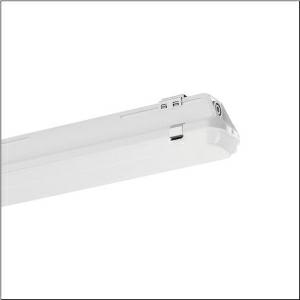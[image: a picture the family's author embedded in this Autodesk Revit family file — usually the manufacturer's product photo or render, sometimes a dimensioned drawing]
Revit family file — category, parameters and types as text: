
# Revit family: monsun_r__12_51fp207p430h_da32
name_source: partatom
category: Lighting Fixtures
units: mm (PartAtom-declared; Revit-internal decimal feet)

## family parameters
Cut with Voids When Loaded = No
Host = Face
Light Source = No
Part Type = Normal
Room Calculation Point = No
Round Connector Dimension = Use Diameter
Shared = No

## types (1)
- Monsun® 12 (1 x LED, 3990 lm, 24.8 W, 4000K)
    Apparent Load = 25 VA
    CIE Flux Codes = 45 75 93 94 100
    Color Rendering = 80
    Color Temperature = 4000K
    Default Elevation = 1800 mm
    Description = Monsun® 12, damp-proof luminaire, chain hanger, primary optical cover: enclosure, of PC, light emission: direct distribution, primary light characteristic: symmetric, installation type: suspended mounting, surface-mounted, horizontal mounting, vertical mounting, LED rated luminous flux: 3.990 lm, light colour: 840, colour temperature: 4000K, control gear: ECG, with terminal, 3-pole, max. 2.5mm², mains connection: 220..240V, AC, 50/60Hz, rated input power: 25W, luminaire housing, of glass-fibre reinforced polyester, uncoated, bright grey, length: 1.590 mm, width: 90 mm, height: 88mm, clip for enclosure, of stainless steel (V2A), ceiling mounting element, of stainless steel (V2A), chain hanger, of stainless steel (V2A), protection rating (complete): IP66, insulation class (complete): insulation class I (protective earthing), certification: CE, ENEC, VDE, protection symbol: D, impact resistance: IK08, permissible ambient temperature for indoor applications: -35..+40°C, standard: EN 50419, EN 60598-2-1, no direct snow, no direct sun, no direct rain, for indoor or canopied outdoor use, corresponds to IFS (International Featured Standards) requirements for safety and quality in the food industry, packaging unit: 1 piece
    Height = 89 mm
    Lamp = 1 x LED
    Lamp Light Flux = 3990 lm
    Lamp Power = 24.8 W
    Lamp count = 1
    Length = 1590 mm
    Luminous efficacy = 161 lm/W
    Manufacturer = Siteco
    ModVariant = No
    Model = 51FP207P430H
    Mounting Place = Ceiling
    Mounting Type = Pendant
    Number of Poles = 1
    OnlyDefault = Yes
    Power Factor = 1
    Product Name = Monsun® 12
    Product group = damp-proof luminaire | ceiling pendant
    ProductGroupID = 908
    Protection Class = Protection class I
    Protection Degree = IP 66
    RLX_Detail_Level = 1
    RlxData = <blob elided: 88305 chars, md5=d8cfdf12>
    Socket = socket
    Standby Power = 0 W
    System Light Flux = 3990 lm
    System Power = 25 W
    Type Comments = Product without accessories
    Type Image = l_1004748.jpg
    URL = http://relux.com
    VarID = ---
    Voltage = 0 V
    Weight = 0.00 kg
    Width = 90 mm

## geometry (parser evidence)
native form markers: Blend x4, Sweep x11
no freeform markers — native parametric forms only
